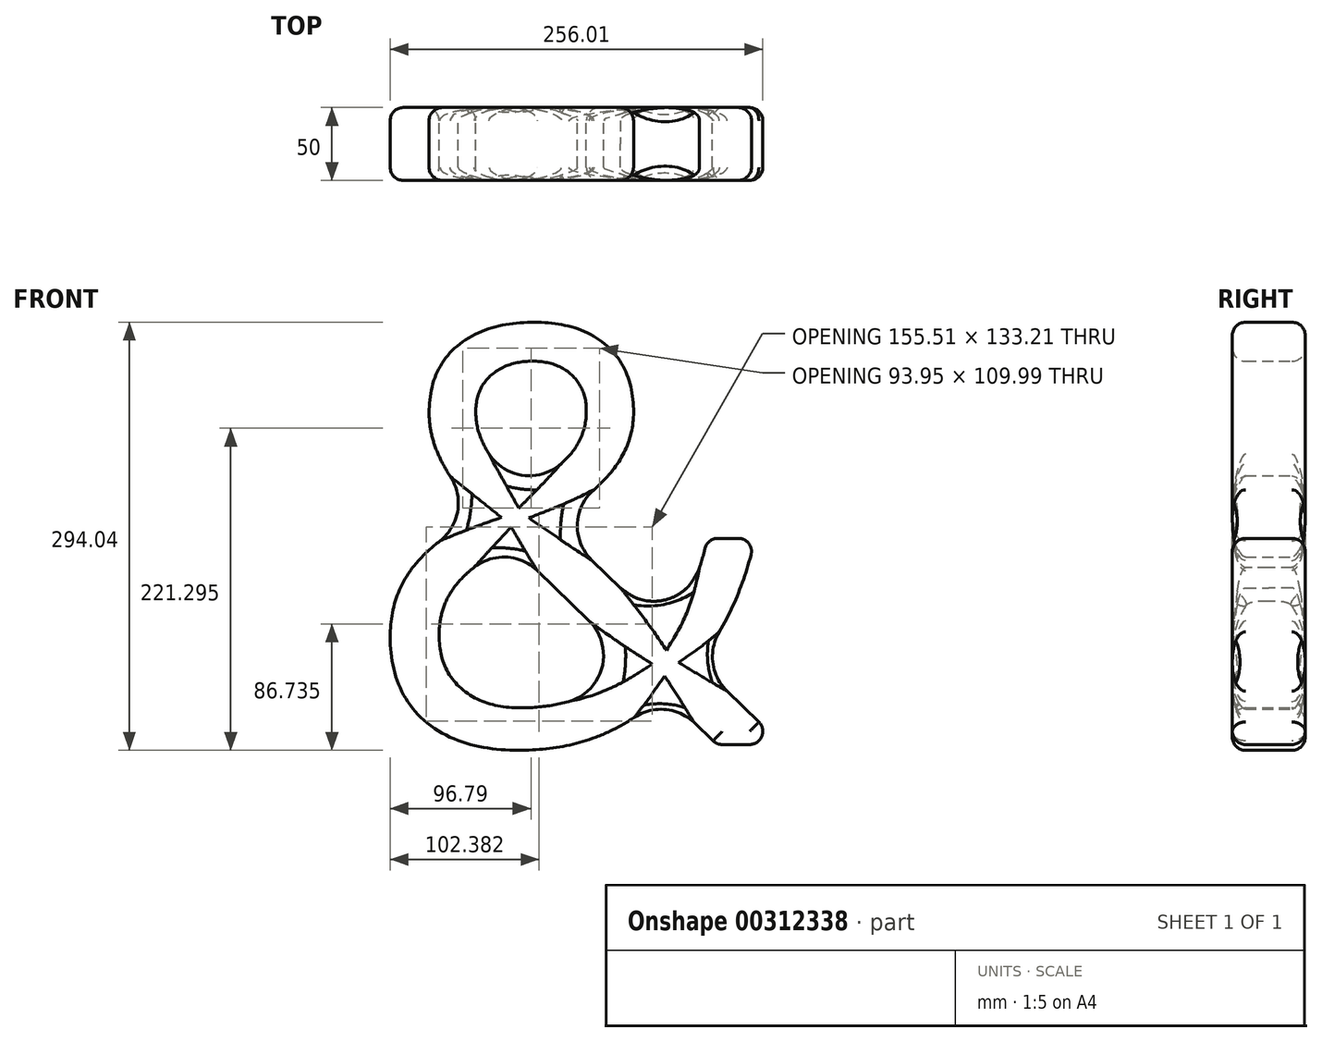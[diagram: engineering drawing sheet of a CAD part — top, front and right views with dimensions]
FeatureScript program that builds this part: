
annotation { "Feature Type Name" : "Feature", "Feature Type Description" : "" }
export const myFeature = defineFeature(function(context is Context, id is Id, definition is map)
    precondition{}
    {
        {
            var Q0;
            Q0=qCreatedBy(makeId("Front.planeOp"),FACE);
            var sketch = newSketch(context, id + "F0", { "sketchPlane" : qUnion([Q0])});
            skText(sketch, "E0", { "text": "&", "fontName": "OpenSans-Regular.ttf"});
            const initialGuessF0  = {"E0": [-0.11236, -0.14734, 1, 0, 0.28804]};
            skSetInitialGuess(sketch, initialGuessF0);
            skSolve(sketch);
        }
        {
            var Q0;
            Q0 = qSketchRegion(id + "F0", true);
            extrude(context, id + "F1", {"entities" : qUnion([Q0]), "depth" : 25 * mm});
        }
        {
            var Q0;
            Q0=makeQuery(id+"F1.opExtrude","CAP_FACE",FACE,{"disambiguationData":[OSD([sQuery(id+"F0.wireOp",EDGE,"E0.sketch_text.stroke-0"),sQuery(id+"F0.wireOp",EDGE,"E0.sketch_text.stroke-1"),sQuery(id+"F0.wireOp",EDGE,"E0.sketch_text.stroke-2"),sQuery(id+"F0.wireOp",EDGE,"E0.sketch_text.stroke-3"),sQuery(id+"F0.wireOp",EDGE,"E0.sketch_text.stroke-4"),sQuery(id+"F0.wireOp",EDGE,"E0.sketch_text.stroke-5"),sQuery(id+"F0.wireOp",EDGE,"E0.sketch_text.stroke-6"),sQuery(id+"F0.wireOp",EDGE,"E0.sketch_text.stroke-7"),sQuery(id+"F0.wireOp",EDGE,"E0.sketch_text.stroke-8"),sQuery(id+"F0.wireOp",EDGE,"E0.sketch_text.stroke-9"),sQuery(id+"F0.wireOp",EDGE,"E0.sketch_text.stroke-10"),sQuery(id+"F0.wireOp",EDGE,"E0.sketch_text.stroke-11"),sQuery(id+"F0.wireOp",EDGE,"E0.sketch_text.stroke-12"),sQuery(id+"F0.wireOp",EDGE,"E0.sketch_text.stroke-13"),sQuery(id+"F0.wireOp",EDGE,"E0.sketch_text.stroke-14"),sQuery(id+"F0.wireOp",EDGE,"E0.sketch_text.stroke-15"),sQuery(id+"F0.wireOp",EDGE,"E0.sketch_text.stroke-16"),sQuery(id+"F0.wireOp",EDGE,"E0.sketch_text.stroke-17"),sQuery(id+"F0.wireOp",EDGE,"E0.sketch_text.stroke-18"),sQuery(id+"F0.wireOp",EDGE,"E0.sketch_text.stroke-19"),sQuery(id+"F0.wireOp",EDGE,"E0.sketch_text.stroke-20"),sQuery(id+"F0.wireOp",EDGE,"E0.sketch_text.stroke-21"),sQuery(id+"F0.wireOp",EDGE,"E0.sketch_text.stroke-22"),sQuery(id+"F0.wireOp",EDGE,"E0.sketch_text.stroke-23"),sQuery(id+"F0.wireOp",EDGE,"E0.sketch_text.stroke-24"),sQuery(id+"F0.wireOp",EDGE,"E0.sketch_text.stroke-25"),sQuery(id+"F0.wireOp",EDGE,"E0.sketch_text.stroke-26"),sQuery(id+"F0.wireOp",EDGE,"E0.sketch_text.stroke-27"),sQuery(id+"F0.wireOp",EDGE,"E0.sketch_text.stroke-28"),sQuery(id+"F0.wireOp",EDGE,"E0.sketch_text.stroke-29"),sQuery(id+"F0.wireOp",EDGE,"E0.sketch_text.stroke-30"),sQuery(id+"F0.wireOp",EDGE,"E0.sketch_text.stroke-31"),sQuery(id+"F0.wireOp",EDGE,"E0.sketch_text.stroke-32"),sQuery(id+"F0.wireOp",EDGE,"E0.sketch_text.stroke-33"),sQuery(id+"F0.wireOp",EDGE,"E0.sketch_text.stroke-34"),sQuery(id+"F0.wireOp",EDGE,"E0.sketch_text.stroke-35"),sQuery(id+"F0.wireOp",EDGE,"E0.sketch_text.stroke-36"),sQuery(id+"F0.wireOp",EDGE,"E0.sketch_text.stroke-37")])],"isStart":false});
            fillet(context, id + "F2", {"entities" : qUnion([Q0]), "radius" : 9 * mm, "tangentPropagation" : true, "allowEdgeOverflow" : false});
        }
        {
            var Q0;
            Q0=makeQuery(id+"F1.opExtrude","SWEPT_EDGE",EDGE,{"disambiguationData":[OSD([sQuery(id+"F0.wireOp",EDGE,"E0.sketch_text.stroke-9"),sQuery(id+"F0.wireOp",EDGE,"E0.sketch_text.stroke-10")])]});
            var Q1;
            Q1=makeQuery(id+"F1.opExtrude","SWEPT_EDGE",EDGE,{"disambiguationData":[OSD([sQuery(id+"F0.wireOp",EDGE,"E0.sketch_text.stroke-25"),sQuery(id+"F0.wireOp",EDGE,"E0.sketch_text.stroke-26")])]});
            var Q2;
            Q2=makeQuery(id+"F1.opExtrude","SWEPT_EDGE",EDGE,{"disambiguationData":[OSD([sQuery(id+"F0.wireOp",EDGE,"E0.sketch_text.stroke-1"),sQuery(id+"F0.wireOp",EDGE,"E0.sketch_text.stroke-2")])]});
            var Q3;
            Q3=makeQuery(id+"F1.opExtrude","SWEPT_EDGE",EDGE,{"disambiguationData":[OSD([sQuery(id+"F0.wireOp",EDGE,"E0.sketch_text.stroke-16"),sQuery(id+"F0.wireOp",EDGE,"E0.sketch_text.stroke-17")])]});
            var Q4;
            Q4=makeQuery(id+"F2.opFillet","BLEND_EDGE",EDGE,{"blendedFrom":[makeQuery(id+"F1.opExtrude","CAP_EDGE",EDGE,{"disambiguationData":[OSD([sQuery(id+"F0.wireOp",EDGE,"E0.sketch_text.stroke-8")])],"isStart":false}),makeQuery(id+"F1.opExtrude","CAP_EDGE",EDGE,{"disambiguationData":[OSD([sQuery(id+"F0.wireOp",EDGE,"E0.sketch_text.stroke-9")])],"isStart":false})],"blendedInto":[]});
            var Q5;
            Q5=makeQuery(id+"F2.opFillet","BLEND_EDGE",EDGE,{"blendedFrom":[makeQuery(id+"F1.opExtrude","CAP_EDGE",EDGE,{"disambiguationData":[OSD([sQuery(id+"F0.wireOp",EDGE,"E0.sketch_text.stroke-26")])],"isStart":false}),makeQuery(id+"F1.opExtrude","CAP_EDGE",EDGE,{"disambiguationData":[OSD([sQuery(id+"F0.wireOp",EDGE,"E0.sketch_text.stroke-27")])],"isStart":false})],"blendedInto":[]});
            var Q6;
            Q6=makeQuery(id+"F2.opFillet","BLEND_EDGE",EDGE,{"blendedFrom":[makeQuery(id+"F1.opExtrude","CAP_EDGE",EDGE,{"disambiguationData":[OSD([sQuery(id+"F0.wireOp",EDGE,"E0.sketch_text.stroke-33")])],"isStart":false}),makeQuery(id+"F1.opExtrude","CAP_EDGE",EDGE,{"disambiguationData":[OSD([sQuery(id+"F0.wireOp",EDGE,"E0.sketch_text.stroke-34")])],"isStart":false})],"blendedInto":[]});
            var Q7;
            Q7=makeQuery(id+"F2.opFillet","BLEND_EDGE",EDGE,{"blendedFrom":[makeQuery(id+"F1.opExtrude","CAP_EDGE",EDGE,{"disambiguationData":[OSD([sQuery(id+"F0.wireOp",EDGE,"E0.sketch_text.stroke-30")])],"isStart":false}),makeQuery(id+"F1.opExtrude","CAP_EDGE",EDGE,{"disambiguationData":[OSD([sQuery(id+"F0.wireOp",EDGE,"E0.sketch_text.stroke-31")])],"isStart":false})],"blendedInto":[]});
            fillet(context, id + "F3", {"entities" : qUnion([Q0, Q1, Q2, Q3, Q4, Q5, Q6, Q7]), "radius" : 33 * mm, "tangentPropagation" : true, "allowEdgeOverflow" : false});
        }
        {
            var Q0;
            Q0=makeQuery(id+"F1.opExtrude","SWEPT_BODY",BODY,{"disambiguationData":[OSD([sQuery(id+"F0.wireOp",EDGE,"E0.sketch_text.stroke-0"),sQuery(id+"F0.wireOp",EDGE,"E0.sketch_text.stroke-1"),sQuery(id+"F0.wireOp",EDGE,"E0.sketch_text.stroke-2"),sQuery(id+"F0.wireOp",EDGE,"E0.sketch_text.stroke-3"),sQuery(id+"F0.wireOp",EDGE,"E0.sketch_text.stroke-4"),sQuery(id+"F0.wireOp",EDGE,"E0.sketch_text.stroke-5"),sQuery(id+"F0.wireOp",EDGE,"E0.sketch_text.stroke-6"),sQuery(id+"F0.wireOp",EDGE,"E0.sketch_text.stroke-7"),sQuery(id+"F0.wireOp",EDGE,"E0.sketch_text.stroke-8"),sQuery(id+"F0.wireOp",EDGE,"E0.sketch_text.stroke-9"),sQuery(id+"F0.wireOp",EDGE,"E0.sketch_text.stroke-10"),sQuery(id+"F0.wireOp",EDGE,"E0.sketch_text.stroke-11"),sQuery(id+"F0.wireOp",EDGE,"E0.sketch_text.stroke-12"),sQuery(id+"F0.wireOp",EDGE,"E0.sketch_text.stroke-13"),sQuery(id+"F0.wireOp",EDGE,"E0.sketch_text.stroke-14"),sQuery(id+"F0.wireOp",EDGE,"E0.sketch_text.stroke-15"),sQuery(id+"F0.wireOp",EDGE,"E0.sketch_text.stroke-16"),sQuery(id+"F0.wireOp",EDGE,"E0.sketch_text.stroke-17"),sQuery(id+"F0.wireOp",EDGE,"E0.sketch_text.stroke-18"),sQuery(id+"F0.wireOp",EDGE,"E0.sketch_text.stroke-19"),sQuery(id+"F0.wireOp",EDGE,"E0.sketch_text.stroke-20"),sQuery(id+"F0.wireOp",EDGE,"E0.sketch_text.stroke-21"),sQuery(id+"F0.wireOp",EDGE,"E0.sketch_text.stroke-22"),sQuery(id+"F0.wireOp",EDGE,"E0.sketch_text.stroke-23"),sQuery(id+"F0.wireOp",EDGE,"E0.sketch_text.stroke-24"),sQuery(id+"F0.wireOp",EDGE,"E0.sketch_text.stroke-25"),sQuery(id+"F0.wireOp",EDGE,"E0.sketch_text.stroke-26"),sQuery(id+"F0.wireOp",EDGE,"E0.sketch_text.stroke-27"),sQuery(id+"F0.wireOp",EDGE,"E0.sketch_text.stroke-28"),sQuery(id+"F0.wireOp",EDGE,"E0.sketch_text.stroke-29"),sQuery(id+"F0.wireOp",EDGE,"E0.sketch_text.stroke-30"),sQuery(id+"F0.wireOp",EDGE,"E0.sketch_text.stroke-31"),sQuery(id+"F0.wireOp",EDGE,"E0.sketch_text.stroke-32"),sQuery(id+"F0.wireOp",EDGE,"E0.sketch_text.stroke-33"),sQuery(id+"F0.wireOp",EDGE,"E0.sketch_text.stroke-34"),sQuery(id+"F0.wireOp",EDGE,"E0.sketch_text.stroke-35"),sQuery(id+"F0.wireOp",EDGE,"E0.sketch_text.stroke-36"),sQuery(id+"F0.wireOp",EDGE,"E0.sketch_text.stroke-37")])]});
            var Q1;
            Q1=qCreatedBy(makeId("Front.planeOp"),FACE);
            mirror(context, id + "F4", {"operationType" : NewBodyOperationType.ADD, "entities" : qUnion([Q0]), "mirrorPlane" : qUnion([Q1])});
        }
        {
            var Q0;
            {var subQ0=makeQuery(id+"F1.opExtrude","SWEPT_EDGE",EDGE,{"disambiguationData":[OSD([sQuery(id+"F0.wireOp",EDGE,"E0.sketch_text.stroke-31"),sQuery(id+"F0.wireOp",EDGE,"E0.sketch_text.stroke-32")])]});Q0=makeQuery(id+"F4.boolean.opBoolean","MERGE",EDGE,{"derivedFrom":[subQ0,makeQuery(id+"F4.opPattern","COPY",EDGE,{"derivedFrom":subQ0,"instanceName":"1"})]});}
            var Q1;
            {var subQ0=makeQuery(id+"F1.opExtrude","SWEPT_EDGE",EDGE,{"disambiguationData":[OSD([sQuery(id+"F0.wireOp",EDGE,"E0.sketch_text.stroke-32"),sQuery(id+"F0.wireOp",EDGE,"E0.sketch_text.stroke-33")])]});Q1=makeQuery(id+"F4.boolean.opBoolean","MERGE",EDGE,{"derivedFrom":[subQ0,makeQuery(id+"F4.opPattern","COPY",EDGE,{"derivedFrom":subQ0,"instanceName":"1"})]});}
            var Q2;
            {var subQ0=makeQuery(id+"F1.opExtrude","SWEPT_EDGE",EDGE,{"disambiguationData":[OSD([sQuery(id+"F0.wireOp",EDGE,"E0.sketch_text.stroke-28"),sQuery(id+"F0.wireOp",EDGE,"E0.sketch_text.stroke-29")])]});Q2=makeQuery(id+"F4.boolean.opBoolean","MERGE",EDGE,{"derivedFrom":[subQ0,makeQuery(id+"F4.opPattern","COPY",EDGE,{"derivedFrom":subQ0,"instanceName":"1"})]});}
            var Q3;
            {var subQ0=makeQuery(id+"F1.opExtrude","SWEPT_EDGE",EDGE,{"disambiguationData":[OSD([sQuery(id+"F0.wireOp",EDGE,"E0.sketch_text.stroke-29"),sQuery(id+"F0.wireOp",EDGE,"E0.sketch_text.stroke-30")])]});Q3=makeQuery(id+"F4.boolean.opBoolean","MERGE",EDGE,{"derivedFrom":[subQ0,makeQuery(id+"F4.opPattern","COPY",EDGE,{"derivedFrom":subQ0,"instanceName":"1"})]});}
            fillet(context, id + "F5", {"entities" : qUnion([Q0, Q1, Q2, Q3]), "radius" : 9 * mm, "tangentPropagation" : true, "allowEdgeOverflow" : false});
        }
    });
